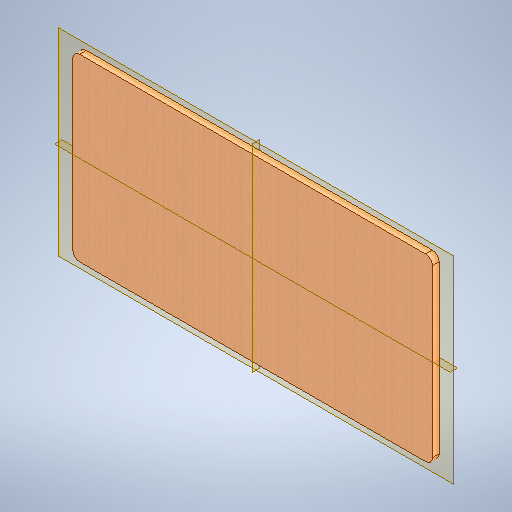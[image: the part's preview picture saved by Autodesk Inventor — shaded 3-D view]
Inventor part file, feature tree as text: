
AUTODESK INVENTOR PART (.ipt)
format: ipt  version: 2025.2 (Build 292293000, 293)  size: 333,824 bytes
history: native  units: mm
features: fillet x4, extrude x2, mirror x2, sketch x2, other x1
ambient origin geometry x8: Origin, YZ Plane, XZ Plane, XY Plane, X Axis, Y Axis, Z Axis, Center Point
bodies: Body1 (feature_tree)
feature tree (11):
  other  "Sólido1"
  extrude  "Extrusão1"  Depth=800.0mm
  fillet  "Arredondamento1"  Radius=30.0mm
  fillet  "Arredondamento2"  Radius=30.0mm
  fillet  "Arredondamento3"  Radius=30.0mm
  fillet  "Arredondamento4"  Radius=30.0mm
  extrude  "Extrusão2"  Depth=15.0mm
  mirror  "Espelhar1"
  mirror  "Espelhar2"
  sketch  "Esboço1"  dims[d0=1600.0mm d1=800.0mm d2=30.0mm d3=0.0mm d4=30.0mm d5=30.0mm d6=30.0mm]
  sketch  "Esboço3"  dims[d7=30.0mm d9=70.8mm d10=350.0mm d11=750.0mm d13=34.2mm d14=15.0mm d15=0.0mm]
